# Revit family: Detail-Shades-Hunter_Douglas-RB500-Heavy_Duty-Auto-Bracket-55L-Pocket_Details
name_source: partatom
category: Detail Items
units: mm (PartAtom-declared; Revit-internal decimal feet)

## family parameters
OmniClass Number = 23.30.60.14
OmniClass Title = Interior Window Treatment
Rotate with component = No
Section Shape = Not Defined
Shared = No

## types (3) — shared parameters
Assembly Code = E2010300
CD_Gypsum Pocket = No
CD_Install Documentation = https://www.hunterdouglasarchitectural.com
CD_Microsite = https://microsite.caddetails.com
CD_Not Ceiling Pocket = Yes
CD_Product Documentation Link = https://www.hunterdouglasarchitectural.com
CD_Product Name = RB 500 Roller Shade System
CD_Product Page URL = https://www.hunterdouglasarchitectural.com
CD_Warranty = https://assets.hunterdouglasarchitectural.com
CD_Width = 5 1/4"
Description = Heavy Duty Automatic Roller Shade
Manufacturer = Hunter Douglas Architectural
Model = Heavy Duty Automatic 55L Bracket
URL = https://www.hunterdouglasarchitectural.com

## per-type parameters (varying)
| type | CD_Height | CD_Surface Pocket | CD_Tile Pocket | Type Comments |
| Ceiling Pocket | 5 7/32" | No | Yes | Tile Pocket |
| Tile Pocket | 5 7/32" | No | Yes | Tile Pocket |
| Surface Pocket | 5 1/4" | Yes | No | Surface Pocket |

## geometry (parser evidence)
native form markers: Sweep x2
no freeform markers — native parametric forms only
